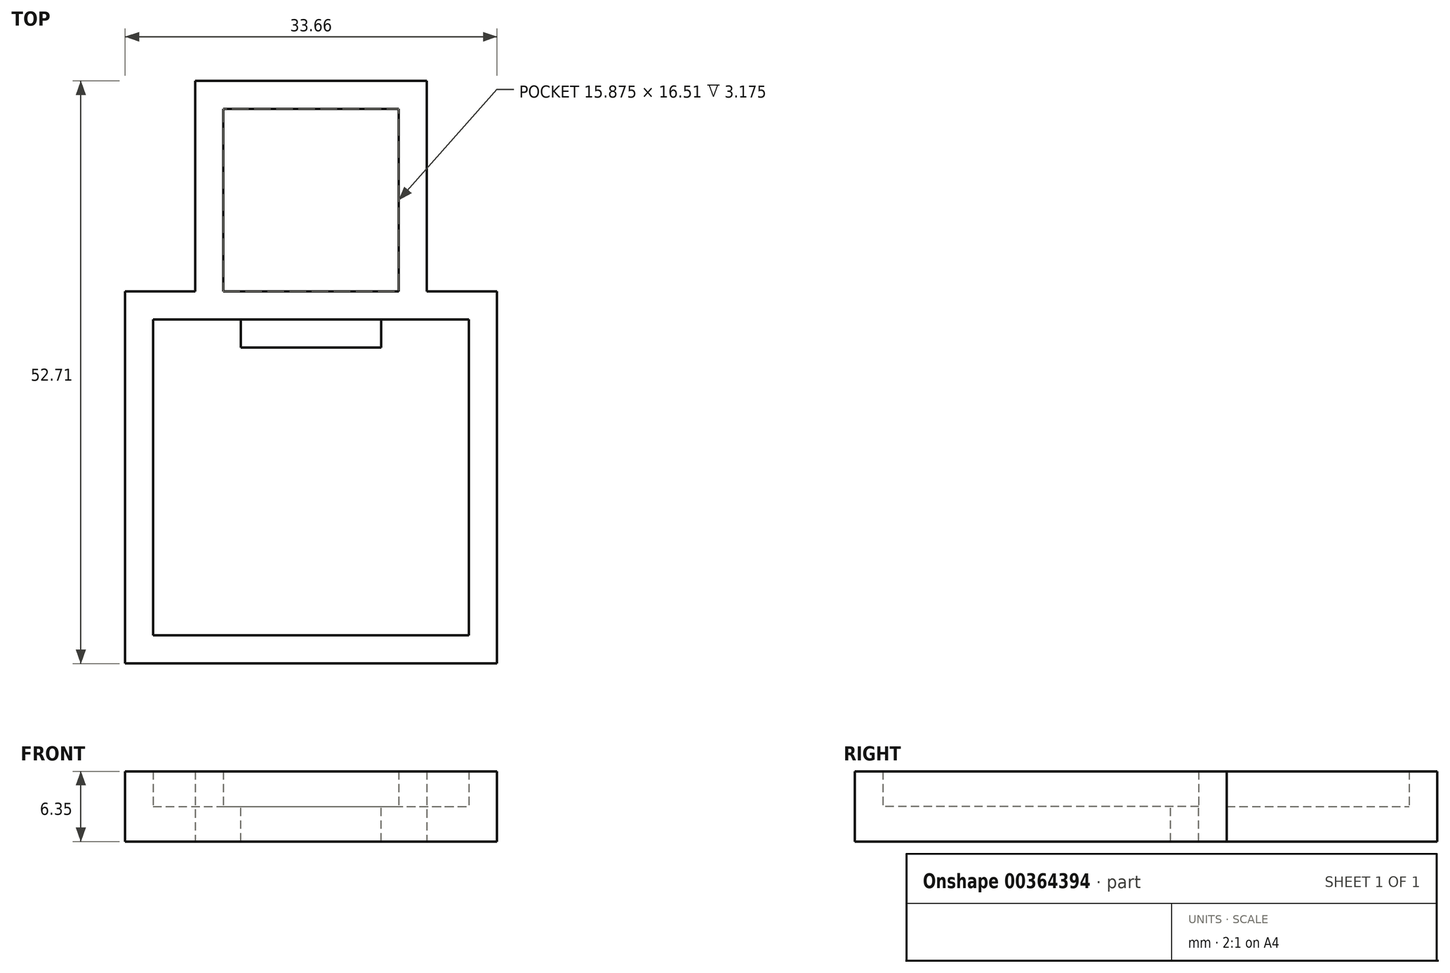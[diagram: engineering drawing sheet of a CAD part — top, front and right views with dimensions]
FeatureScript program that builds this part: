
annotation { "Feature Type Name" : "Feature", "Feature Type Description" : "" }
export const myFeature = defineFeature(function(context is Context, id is Id, definition is map)
    precondition{}
    {
        {
            var Q0;
            Q0=qCreatedBy(makeId("Top.planeOp"),FACE);
            cPlane(context, id + "F0", {"entities" : qUnion([Q0]), "cplaneType" : CPlaneType.OFFSET, "offset" : 0 * mm, "width" : 152.4 * mm, "height" : 152.4 * mm});
        }
        {
            var Q0;
            Q0=qCreatedBy(id+"F0.planeOp",FACE);
            var sketch = newSketch(context, id + "F1", { "sketchPlane" : qUnion([Q0])});
            skLineSegment(sketch, "E0.bottom", {"start": v(-14.29, 14.29) * mm, "end": v(-7.94, 14.29) * mm});
            skLineSegment(sketch, "E0.top", {"start": v(-14.29, -14.29) * mm, "end": v(14.29, -14.29) * mm});
            skLineSegment(sketch, "E0.left", {"start": v(-14.29, 14.29) * mm, "end": v(-14.29, -14.29) * mm});
            skLineSegment(sketch, "E0.right", {"start": v(14.29, 14.29) * mm, "end": v(14.29, -14.29) * mm});
            skLineSegment(sketch, "E1.top", {"start": v(-7.94, 33.34) * mm, "end": v(7.94, 33.34) * mm});
            skLineSegment(sketch, "E1.left", {"start": v(-7.94, 14.29) * mm, "end": v(-7.94, 33.34) * mm});
            skLineSegment(sketch, "E1.right", {"start": v(7.94, 14.29) * mm, "end": v(7.94, 33.34) * mm});
            skLineSegment(sketch, "E2.trimOffspring", {"start": v(7.94, 14.29) * mm, "end": v(14.29, 14.29) * mm});
            skSolve(sketch);
        }
        {
            var Q0;
            Q0=makeQuery(id+"F1.imprint","IMPRINT",FACE,{"disambiguationData":[TD([[makeQuery(id+"F1.imprint","IMPRINT",EDGE,{"derivedFrom":sQuery(id+"F1.wireOp",EDGE,"E0.bottom")}),-1.0]])]});
            extrude(context, id + "F2", {"entities" : qUnion([Q0]), "depth" : 3.17 * mm});
        }
        {
            var Q0;
            Q0=makeQuery(id+"F2.opExtrude","CAP_FACE",FACE,{"disambiguationData":[OSD([sQuery(id+"F1.wireOp",EDGE,"E0.bottom"),sQuery(id+"F1.wireOp",EDGE,"E0.top"),sQuery(id+"F1.wireOp",EDGE,"E0.left"),sQuery(id+"F1.wireOp",EDGE,"E0.right"),sQuery(id+"F1.wireOp",EDGE,"E1.top"),sQuery(id+"F1.wireOp",EDGE,"E1.left"),sQuery(id+"F1.wireOp",EDGE,"E1.right"),sQuery(id+"F1.wireOp",EDGE,"E2.trimOffspring")])],"isStart":true});
            var sketch = newSketch(context, id + "F3", { "sketchPlane" : qUnion([Q0])});
            skLineSegment(sketch, "E3.bottom", {"start": v(14.29, 14.29) * mm, "end": v(-14.29, 14.29) * mm});
            skLineSegment(sketch, "E3.top", {"start": v(14.29, -14.29) * mm, "end": v(7.94, -14.29) * mm});
            skLineSegment(sketch, "E3.left", {"start": v(14.29, 14.29) * mm, "end": v(14.29, -14.29) * mm});
            skLineSegment(sketch, "E3.right", {"start": v(-14.29, 14.29) * mm, "end": v(-14.29, -14.29) * mm});
            skLineSegment(sketch, "E4", {"start": v(7.94, -14.29) * mm, "end": v(7.94, -33.34) * mm});
            skLineSegment(sketch, "E5", {"start": v(7.94, -33.34) * mm, "end": v(-7.94, -33.34) * mm});
            skLineSegment(sketch, "E6", {"start": v(-7.94, -33.34) * mm, "end": v(-7.94, -14.29) * mm});
            skLineSegment(sketch, "E7.trimOffspring", {"start": v(-7.94, -14.29) * mm, "end": v(-14.29, -14.29) * mm});
            skLineSegment(sketch, "E8.0", {"start": v(16.83, 16.83) * mm, "end": v(16.83, -16.83) * mm});
            skLineSegment(sketch, "E8.1", {"start": v(-16.83, 16.83) * mm, "end": v(16.83, 16.83) * mm});
            skLineSegment(sketch, "E8.2", {"start": v(16.83, -16.83) * mm, "end": v(10.48, -16.83) * mm});
            skLineSegment(sketch, "E8.3", {"start": v(-16.83, -16.83) * mm, "end": v(-16.83, 16.83) * mm});
            skLineSegment(sketch, "E8.4", {"start": v(10.48, -16.83) * mm, "end": v(10.48, -35.88) * mm});
            skLineSegment(sketch, "E8.5", {"start": v(10.48, -35.88) * mm, "end": v(-10.48, -35.88) * mm});
            skLineSegment(sketch, "E8.6", {"start": v(-10.48, -35.88) * mm, "end": v(-10.48, -16.83) * mm});
            skLineSegment(sketch, "E8.7", {"start": v(-10.48, -16.83) * mm, "end": v(-16.83, -16.83) * mm});
            skSolve(sketch);
        }
        {
            var Q0;
            Q0=makeQuery(id+"F3.imprint","IMPRINT",FACE,{"disambiguationData":[TD([[makeQuery(id+"F3.imprint","IMPRINT",EDGE,{"derivedFrom":sQuery(id+"F3.wireOp",EDGE,"E3.bottom")}),1.0]])]});
            extrude(context, id + "F4", {"entities" : qUnion([Q0]), "operationType" : NewBodyOperationType.ADD, "oppositeDirection" : true, "depth" : 6.35 * mm});
        }
        {
            var Q0;
            Q0=makeQuery(id+"F2.opExtrude","CAP_FACE",FACE,{"disambiguationData":[OSD([sQuery(id+"F1.wireOp",EDGE,"E0.bottom"),sQuery(id+"F1.wireOp",EDGE,"E0.top"),sQuery(id+"F1.wireOp",EDGE,"E0.left"),sQuery(id+"F1.wireOp",EDGE,"E0.right"),sQuery(id+"F1.wireOp",EDGE,"E1.top"),sQuery(id+"F1.wireOp",EDGE,"E1.left"),sQuery(id+"F1.wireOp",EDGE,"E1.right"),sQuery(id+"F1.wireOp",EDGE,"E2.trimOffspring")])],"isStart":false});
            var sketch = newSketch(context, id + "F5", { "sketchPlane" : qUnion([Q0])});
            skLineSegment(sketch, "E9.bottom", {"start": v(-7.94, 14.29) * mm, "end": v(7.94, 14.29) * mm});
            skLineSegment(sketch, "E9.top", {"start": v(-7.94, 16.83) * mm, "end": v(7.94, 16.83) * mm});
            skLineSegment(sketch, "E9.left", {"start": v(-7.94, 14.29) * mm, "end": v(-7.94, 16.83) * mm});
            skLineSegment(sketch, "E9.right", {"start": v(7.94, 14.29) * mm, "end": v(7.94, 16.83) * mm});
            skSolve(sketch);
        }
        {
            var Q0;
            Q0=makeQuery(id+"F5.imprint","IMPRINT",FACE,{"disambiguationData":[TD([[makeQuery(id+"F5.imprint","IMPRINT",EDGE,{"derivedFrom":sQuery(id+"F5.wireOp",EDGE,"E9.bottom")}),1.0]])]});
            var Q1;
            Q1=makeQuery(id+"F4.opExtrude","CAP_FACE",FACE,{"disambiguationData":[OSD([sQuery(id+"F3.wireOp",EDGE,"E3.bottom"),sQuery(id+"F3.wireOp",EDGE,"E3.top"),sQuery(id+"F3.wireOp",EDGE,"E3.left"),sQuery(id+"F3.wireOp",EDGE,"E3.right"),sQuery(id+"F3.wireOp",EDGE,"E4"),sQuery(id+"F3.wireOp",EDGE,"E5"),sQuery(id+"F3.wireOp",EDGE,"E6"),sQuery(id+"F3.wireOp",EDGE,"E7.trimOffspring"),sQuery(id+"F3.wireOp",EDGE,"E8.0"),sQuery(id+"F3.wireOp",EDGE,"E8.1"),sQuery(id+"F3.wireOp",EDGE,"E8.2"),sQuery(id+"F3.wireOp",EDGE,"E8.3"),sQuery(id+"F3.wireOp",EDGE,"E8.4"),sQuery(id+"F3.wireOp",EDGE,"E8.5"),sQuery(id+"F3.wireOp",EDGE,"E8.6"),sQuery(id+"F3.wireOp",EDGE,"E8.7")])],"isStart":false});
            extrude(context, id + "F6", {"entities" : qUnion([Q0]), "operationType" : NewBodyOperationType.ADD, "endBound" : BoundingType.UP_TO_SURFACE, "endBoundEntityFace" : qUnion([Q1]), "depth" : 25.4 * mm});
        }
        {
            var Q0;
            Q0=makeQuery(id+"F6.boolean.opBoolean","SPLIT",FACE,{"disambiguationData":[TD([makeQuery(id+"F4.opExtrude","SWEPT_FACE",FACE,{"disambiguationData":[OSD([sQuery(id+"F3.wireOp",EDGE,"E3.bottom")])]})])],"derivedFrom":makeQuery(id+"F2.opExtrude","CAP_FACE",FACE,{"disambiguationData":[OSD([sQuery(id+"F1.wireOp",EDGE,"E0.bottom"),sQuery(id+"F1.wireOp",EDGE,"E0.top"),sQuery(id+"F1.wireOp",EDGE,"E0.left"),sQuery(id+"F1.wireOp",EDGE,"E0.right"),sQuery(id+"F1.wireOp",EDGE,"E1.top"),sQuery(id+"F1.wireOp",EDGE,"E1.left"),sQuery(id+"F1.wireOp",EDGE,"E1.right"),sQuery(id+"F1.wireOp",EDGE,"E2.trimOffspring")])],"isStart":false})});
            var sketch = newSketch(context, id + "F7", { "sketchPlane" : qUnion([Q0])});
            skLineSegment(sketch, "E10.bottom", {"start": v(-6.35, 14.29) * mm, "end": v(6.35, 14.29) * mm});
            skLineSegment(sketch, "E10.top", {"start": v(-6.35, 11.75) * mm, "end": v(6.35, 11.75) * mm});
            skLineSegment(sketch, "E10.left", {"start": v(-6.35, 14.29) * mm, "end": v(-6.35, 11.75) * mm});
            skLineSegment(sketch, "E10.right", {"start": v(6.35, 14.29) * mm, "end": v(6.35, 11.75) * mm});
            skSolve(sketch);
        }
        {
            var Q0;
            Q0=makeQuery(id+"F7.imprint","IMPRINT",FACE,{"disambiguationData":[TD([[makeQuery(id+"F7.imprint","IMPRINT",EDGE,{"derivedFrom":sQuery(id+"F7.wireOp",EDGE,"E10.bottom")}),-1.0]])]});
            extrude(context, id + "F8", {"entities" : qUnion([Q0]), "operationType" : NewBodyOperationType.REMOVE, "oppositeDirection" : true, "depth" : 25.4 * mm});
        }
    });
